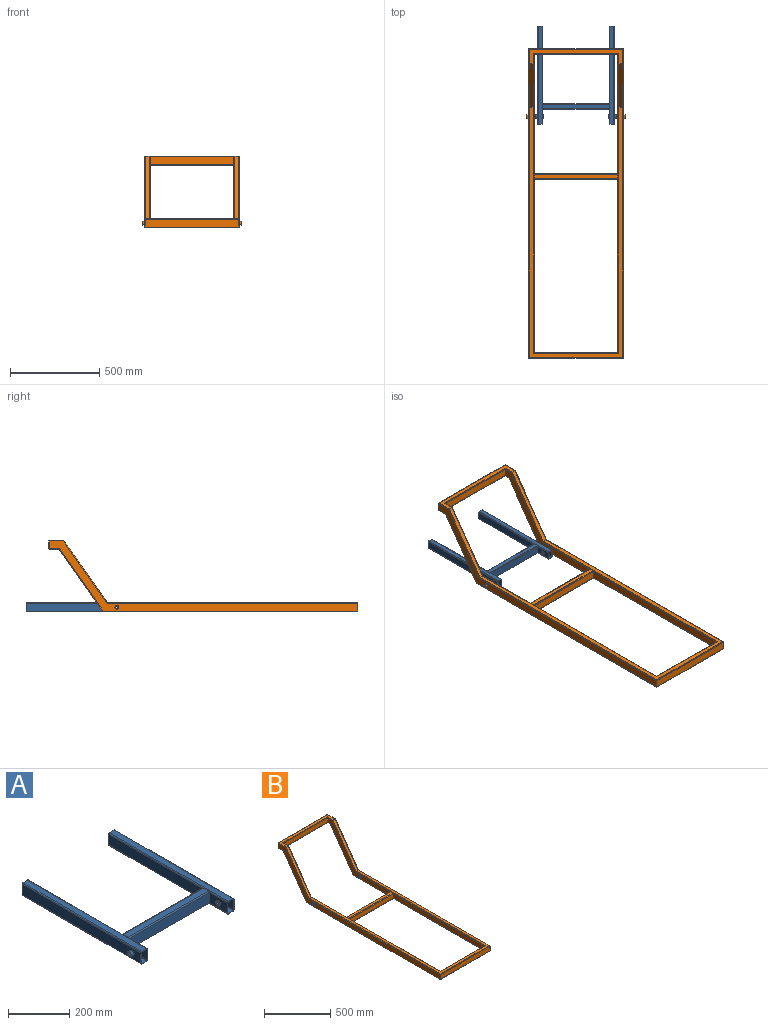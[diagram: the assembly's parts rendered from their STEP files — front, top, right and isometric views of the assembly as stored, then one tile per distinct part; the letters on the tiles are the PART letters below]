
ASSEMBLY  parts=2 mates=1
PART A: 72 faces, bbox 454x550x50 mm
  f0: plane 42x26mm, normal (1,0,0), area 1092mm2, adj f17,f19,f44,f48
  f1: plane 85x42mm, normal (1,0,0), area 3255.8mm2, adj f10,f17,f19,f56,f70
  f2: plane 550x22mm, normal (0,0,-1), area 12100mm2, adj f3,f9,f10,f11
  f3: cylinder r=2.02mm len=550mm, axis (0,1,0), area 1723.3mm2, adj f2,f4,f10,f11
  f4: plane 550x42mm, normal (1,0,0), area 22785.8mm2, adj f3,f5,f10,f11,f71
  f5: cylinder r=2.02mm len=550mm, axis (0,1,0), area 1723.3mm2, adj f4,f6,f10,f11
  f6: plane 550x22mm, normal (0,0,1), area 12100mm2, adj f5,f7,f10,f11
  f7: cylinder r=2.02mm len=550mm, axis (0,1,0), area 1723.3mm2, adj f6,f8,f10,f11
  f8: plane 550x42mm, normal (-1,0,0), area 22785.8mm2, adj f7,f9,f10,f11,f71
  f9: cylinder r=2.02mm len=550mm, axis (0,1,0), area 1723.3mm2, adj f2,f8,f10,f11
  f10: plane 50x30mm, normal (0,-1,0), area 293.8mm2, adj f1,f2,f3,f4,f5,f6,f7,f8
  f11: plane 50x30mm, normal (0,1,0), area 293.8mm2, adj f2,f3,f4,f5,f6,f7,f8,f9
  f12: plane 550x22mm, normal (0,0,-1), area 12100mm2, adj f10,f11,f13,f19
  f13: cylinder r=4mm len=550mm, axis (0,1,0), area 3455.7mm2, adj f10,f11,f12,f14
  f14: plane 550x42mm, normal (-1,0,0), area 22785.8mm2, adj f10,f11,f13,f15,f68
  f15: cylinder r=4mm len=550mm, axis (0,1,0), area 3455.7mm2, adj f10,f11,f14,f16
  f16: plane 550x22mm, normal (0,0,1), area 12100mm2, adj f10,f11,f15,f17
  f17: cylinder r=4mm len=550mm, axis (0,1,0), area 3455.7mm2, adj f0,f1,f10,f11,f16,f18,f58
  f18: plane 435x42mm, normal (1,0,0), area 18270mm2, adj f11,f17,f19,f52
  f19: cylinder r=4mm len=550mm, axis (0,1,0), area 3455.7mm2, adj f0,f1,f10,f11,f12,f18,f20
  f20: plane 30x4mm, normal (-1,0,0), area 62.9mm2, adj f19,f45,f46,f47,f50,f51,f57
  f21: plane 42x26mm, normal (-1,0,0), area 1092mm2, adj f34,f36,f44,f48
  f22: plane 435x42mm, normal (-1,0,0), area 18270mm2, adj f32,f34,f36,f52
  f23: plane 550x22mm, normal (0,0,-1), area 12100mm2, adj f24,f30,f31,f32
  f24: cylinder r=2.02mm len=550mm, axis (0,1,0), area 1723.3mm2, adj f23,f25,f31,f32
  f25: plane 550x42mm, normal (1,0,0), area 22785.8mm2, adj f24,f26,f31,f32,f65
  f26: cylinder r=2.02mm len=550mm, axis (0,1,0), area 1723.3mm2, adj f25,f27,f31,f32
  f27: plane 550x22mm, normal (0,0,1), area 12100mm2, adj f26,f28,f31,f32
  f28: cylinder r=2.02mm len=550mm, axis (0,1,0), area 1723.3mm2, adj f27,f29,f31,f32
  f29: plane 550x42mm, normal (-1,0,0), area 22785.8mm2, adj f28,f30,f31,f32,f65
  f30: cylinder r=2.02mm len=550mm, axis (0,1,0), area 1723.3mm2, adj f23,f29,f31,f32
  f31: plane 50x30mm, normal (0,-1,0), area 293.8mm2, adj f23,f24,f25,f26,f27,f28,f29,f30
  f32: plane 50x30mm, normal (0,1,0), area 293.8mm2, adj f22,f23,f24,f25,f26,f27,f28,f29
  f33: plane 550x22mm, normal (0,0,-1), area 12100mm2, adj f31,f32,f34,f40
  f34: cylinder r=4mm len=550mm, axis (0,1,0), area 3455.7mm2, adj f21,f22,f31,f32,f33,f35,f59
  f35: plane 85x42mm, normal (-1,0,0), area 3255.8mm2, adj f31,f34,f36,f56,f64
  f36: cylinder r=4mm len=550mm, axis (0,1,0), area 3455.7mm2, adj f21,f22,f31,f32,f35,f37,f41
  f37: plane 550x22mm, normal (0,0,1), area 12100mm2, adj f31,f32,f36,f38
  f38: cylinder r=4mm len=550mm, axis (0,1,0), area 3455.7mm2, adj f31,f32,f37,f39
  f39: plane 550x42mm, normal (1,0,0), area 22785.8mm2, adj f31,f32,f38,f40,f62
  f40: cylinder r=4mm len=550mm, axis (0,1,0), area 3455.7mm2, adj f31,f32,f33,f39
  f41: plane 30x4mm, normal (1,0,0), area 62.9mm2, adj f36,f42,f43,f49,f53,f54,f55
  f42: plane 370x22mm, normal (0,0,-1), area 8140mm2, adj f41,f43,f49,f58
  f43: cylinder r=2.02mm len=370mm, axis (1,0,0), area 1159.3mm2, adj f41,f42,f44,f58
  f44: plane 370x42mm, normal (0,-1,0), area 15540mm2, adj f0,f21,f43,f45
  f45: cylinder r=2.02mm len=370mm, axis (1,0,0), area 1159.3mm2, adj f20,f44,f46,f59
  f46: plane 370x22mm, normal (0,0,1), area 8140mm2, adj f20,f45,f47,f59
  f47: cylinder r=2.02mm len=370mm, axis (1,0,0), area 1159.3mm2, adj f20,f46,f48,f59
  f48: plane 370x42mm, normal (0,1,0), area 15540mm2, adj f0,f21,f47,f49
  f49: cylinder r=2.02mm len=370mm, axis (1,0,0), area 1159.3mm2, adj f41,f42,f48,f58
  f50: plane 370x22mm, normal (0,0,-1), area 8140mm2, adj f20,f51,f57,f59
  f51: cylinder r=4mm len=370mm, axis (1,0,0), area 2324.8mm2, adj f20,f50,f52,f59
  f52: plane 370x42mm, normal (0,1,0), area 15540mm2, adj f18,f22,f51,f53
  f53: cylinder r=4mm len=370mm, axis (1,0,0), area 2324.8mm2, adj f41,f52,f54,f58
  f54: plane 370x22mm, normal (0,0,1), area 8140mm2, adj f41,f53,f55,f58
  f55: cylinder r=4mm len=370mm, axis (1,0,0), area 2324.8mm2, adj f41,f54,f56,f58
  f56: plane 370x42mm, normal (0,-1,0), area 15540mm2, adj f1,f35,f55,f57
  f57: cylinder r=4mm len=370mm, axis (1,0,0), area 2324.8mm2, adj f20,f50,f56,f59
  f58: plane 30x4mm, normal (-1,0,0), area 62.9mm2, adj f17,f42,f43,f49,f53,f54,f55
  f59: plane 30x4mm, normal (1,0,0), area 62.9mm2, adj f34,f45,f46,f47,f50,f51,f57
  f60: plane 20x20mm, normal (1,0,0), area 201.1mm2, adj f62,f63
  f61: plane 20x20mm, normal (-1,0,0), area 201.1mm2, adj f63,f64
  f62: cylinder r=10mm len=20mm, axis (1,0,0), area 754mm2, adj f39,f60
  f63: cylinder r=6mm len=45mm, axis (1,0,0), area 1696.5mm2, adj f60,f61
  f64: cylinder r=10mm len=20mm, axis (1,0,0), area 188.5mm2, adj f35,f61
  f65: cylinder r=10mm len=26mm, axis (1,0,0), area 1633.6mm2, adj f25,f29
  f66: plane 20x20mm, normal (-1,0,0), area 201.1mm2, adj f68,f69
  f67: plane 20x20mm, normal (1,0,0), area 201.1mm2, adj f69,f70
  f68: cylinder r=10mm len=20mm, axis (-1,0,0), area 754mm2, adj f14,f66
  f69: cylinder r=6mm len=45mm, axis (-1,0,0), area 1696.5mm2, adj f66,f67
  f70: cylinder r=10mm len=20mm, axis (-1,0,0), area 188.5mm2, adj f1,f67
  f71: cylinder r=10mm len=26mm, axis (-1,0,0), area 1633.6mm2, adj f4,f8
PART B: 132 faces, bbox 550x1730x400 mm
  f0: plane 42x26mm, normal (1,0,0), area 1092mm2, adj f8,f9,f26,f30
  f1: plane 970x42mm, normal (1,0,0), area 40740mm2, adj f8,f9,f18,f71
  f2: plane 670x392mm, normal (1,0,0), area 35478.2mm2, adj f8,f9,f22,f34,f35,f40,f41,f45
  f3: plane 1424.01x522mm, normal (0,0,-1), area 73172.6mm2, adj f4,f9,f39,f61,f62,f66,f70,f75
  f4: cylinder r=4mm len=1428.01mm, axis (0,1,0), area 8958.5mm2, adj f3,f5,f38,f75
  f5: plane 1730x392mm, normal (-1,0,0), area 79998.2mm2, adj f4,f6,f37,f38,f42,f43,f48,f74
  f6: cylinder r=4mm len=1404.07mm, axis (0,1,0), area 8804.5mm2, adj f5,f7,f37,f73
  f7: plane 1397.99x522mm, normal (0,0,1), area 72027.4mm2, adj f6,f8,f36,f58,f63,f64,f72,f73
  f8: cylinder r=4mm len=1378.07mm, axis (0,1,0), area 8634.3mm2, adj f0,f1,f2,f7,f16,f35,f72
  f9: cylinder r=4mm len=1402.01mm, axis (0,1,0), area 8788.3mm2, adj f0,f1,f2,f3,f34,f70,f76
  f10: cylinder r=10mm len=20mm, axis (1,0,0), area 314.2mm2, adj f13,f68
  f11: cylinder r=6mm len=45mm, axis (1,0,0), area 1696.5mm2, adj f13,f14
  f12: cylinder r=10mm len=20mm, axis (1,0,0), area 628.3mm2, adj f14,f65
  f13: plane 20x20mm, normal (-1,0,0), area 201.1mm2, adj f10,f11
  f14: plane 20x20mm, normal (1,0,0), area 201.1mm2, adj f11,f12
  f15: plane 30x4mm, normal (1,0,0), area 62.9mm2, adj f19,f20,f21,f25,f31,f32,f63
  f16: plane 30x4mm, normal (-1,0,0), area 62.9mm2, adj f8,f19,f20,f21,f25,f31,f32
  f17: cylinder r=4mm len=470mm, axis (1,0,0), area 2953.1mm2, adj f18,f24,f33,f76
  f18: plane 470x42mm, normal (0,-1,0), area 19740mm2, adj f1,f17,f19,f67
  f19: cylinder r=4mm len=470mm, axis (1,0,0), area 2953.1mm2, adj f15,f16,f18,f20
  f20: plane 470x22mm, normal (0,0,1), area 10340mm2, adj f15,f16,f19,f21
  f21: cylinder r=4mm len=470mm, axis (1,0,0), area 2953.1mm2, adj f15,f16,f20,f22
  f22: plane 470x42mm, normal (0,1,0), area 19740mm2, adj f2,f21,f23,f68
  f23: cylinder r=4mm len=470mm, axis (1,0,0), area 2953.1mm2, adj f22,f24,f33,f76
  f24: plane 470x22mm, normal (0,0,-1), area 10340mm2, adj f17,f23,f33,f76
  f25: cylinder r=2.02mm len=470mm, axis (1,0,0), area 1472.6mm2, adj f15,f16,f26,f32
  f26: plane 470x42mm, normal (0,1,0), area 19740mm2, adj f0,f25,f27,f69
  f27: cylinder r=2.02mm len=470mm, axis (1,0,0), area 1472.6mm2, adj f26,f28,f33,f76
  f28: plane 470x22mm, normal (0,0,1), area 10340mm2, adj f27,f29,f33,f76
  f29: cylinder r=2.02mm len=470mm, axis (1,0,0), area 1472.6mm2, adj f28,f30,f33,f76
  f30: plane 470x42mm, normal (0,-1,0), area 19740mm2, adj f0,f29,f31,f69
  f31: cylinder r=2.02mm len=470mm, axis (1,0,0), area 1472.6mm2, adj f15,f16,f30,f32
  f32: plane 470x22mm, normal (0,0,-1), area 10340mm2, adj f15,f16,f25,f31
  f33: plane 30x4mm, normal (1,0,0), area 62.9mm2, adj f17,f23,f24,f27,f28,f29,f62
  f34: cylinder r=4mm len=354mm, axis (0,0.57,0.82), area 2684.6mm2, adj f2,f9,f39,f40
  f35: cylinder r=4mm len=354mm, axis (0,0.57,0.82), area 2684.6mm2, adj f2,f8,f36,f41
  f36: plane 350x245.07mm, normal (0,-0.82,0.57), area 9400mm2, adj f7,f35,f37,f52
  f37: cylinder r=4mm len=354mm, axis (0,0.57,0.82), area 2684.6mm2, adj f5,f6,f36,f42
  f38: cylinder r=4mm len=354mm, axis (0,0.57,0.82), area 2684.6mm2, adj f4,f5,f39,f43
  f39: plane 350x245.07mm, normal (0,0.82,-0.57), area 9400mm2, adj f3,f34,f38,f55
  f40: cylinder r=4mm len=33mm, axis (0,1,0), area 183mm2, adj f2,f34,f44,f55
  f41: cylinder r=4mm len=56.94mm, axis (0,1,0), area 337mm2, adj f2,f35,f46,f52
  f42: cylinder r=4mm len=82.94mm, axis (0,1,0), area 507.2mm2, adj f5,f37,f47,f52
  f43: cylinder r=4mm len=59mm, axis (0,1,0), area 353.2mm2, adj f5,f38,f49,f55
  f44: cylinder r=4mm len=478mm, axis (1,0,0), area 2971.3mm2, adj f40,f45,f50,f55
  f45: plane 470x42mm, normal (0,-1,0), area 19740mm2, adj f2,f44,f46,f68
  f46: cylinder r=4mm len=478mm, axis (1,0,0), area 2971.3mm2, adj f41,f45,f51,f52
  f47: cylinder r=4mm len=530mm, axis (1,0,0), area 3311.8mm2, adj f42,f48,f52,f53
  f48: plane 530x42mm, normal (0,1,0), area 22260mm2, adj f5,f47,f49,f65
  f49: cylinder r=4mm len=530mm, axis (1,0,0), area 3311.8mm2, adj f43,f48,f54,f55
  f50: cylinder r=4mm len=33mm, axis (0,-1,0), area 183mm2, adj f44,f55,f56,f68
  f51: cylinder r=4mm len=56.94mm, axis (0,-1,0), area 337mm2, adj f46,f52,f57,f68
  f52: plane 522x78.94mm, normal (0,0,1), area 13989.4mm2, adj f36,f41,f42,f46,f47,f51,f53,f58
  f53: cylinder r=4mm len=82.94mm, axis (0,-1,0), area 507.2mm2, adj f47,f52,f59,f65
  f54: cylinder r=4mm len=59mm, axis (0,-1,0), area 353.2mm2, adj f49,f55,f60,f65
  f55: plane 522x52.91mm, normal (0,0,-1), area 12844.2mm2, adj f39,f40,f43,f44,f49,f50,f54,f61
  f56: cylinder r=4mm len=354mm, axis (0,-0.57,-0.82), area 2684.6mm2, adj f50,f61,f62,f68
  f57: cylinder r=4mm len=354mm, axis (0,-0.57,-0.82), area 2684.6mm2, adj f51,f58,f63,f68
  f58: plane 350x245.07mm, normal (0,-0.82,0.57), area 9400mm2, adj f7,f52,f57,f59
  f59: cylinder r=4mm len=354mm, axis (0,-0.57,-0.82), area 2684.6mm2, adj f53,f58,f64,f65
  f60: cylinder r=4mm len=354mm, axis (0,-0.57,-0.82), area 2684.6mm2, adj f54,f61,f65,f66
  f61: plane 350x245.07mm, normal (0,0.82,-0.57), area 9400mm2, adj f3,f55,f56,f60
  f62: cylinder r=4mm len=1402.01mm, axis (0,-1,0), area 8788.3mm2, adj f3,f33,f56,f67,f68,f69,f70
  f63: cylinder r=4mm len=1378.07mm, axis (0,-1,0), area 8634.3mm2, adj f7,f15,f57,f67,f68,f69,f72
  f64: cylinder r=4mm len=1404.07mm, axis (0,-1,0), area 8804.5mm2, adj f7,f59,f65,f73
  f65: plane 1730x392mm, normal (1,0,0), area 79998.2mm2, adj f12,f48,f53,f54,f59,f60,f64,f66
  f66: cylinder r=4mm len=1428.01mm, axis (0,-1,0), area 8958.5mm2, adj f3,f60,f65,f75
  f67: plane 970x42mm, normal (-1,0,0), area 40740mm2, adj f18,f62,f63,f71
  f68: plane 670x392mm, normal (-1,0,0), area 35478.2mm2, adj f10,f22,f45,f50,f51,f56,f57,f62
  f69: plane 42x26mm, normal (-1,0,0), area 1092mm2, adj f26,f30,f62,f63
  f70: cylinder r=4mm len=478mm, axis (-1,0,0), area 2971.3mm2, adj f3,f9,f62,f71
  f71: plane 470x42mm, normal (0,1,0), area 19740mm2, adj f1,f67,f70,f72
  f72: cylinder r=4mm len=478mm, axis (-1,0,0), area 2971.3mm2, adj f7,f8,f63,f71
  f73: cylinder r=4mm len=530mm, axis (-1,0,0), area 3311.8mm2, adj f6,f7,f64,f74
  f74: plane 530x42mm, normal (0,-1,0), area 22260mm2, adj f5,f65,f73,f75
  f75: cylinder r=4mm len=530mm, axis (-1,0,0), area 3311.8mm2, adj f3,f4,f66,f74
  f76: plane 30x4mm, normal (-1,0,0), area 62.9mm2, adj f9,f17,f23,f24,f27,f28,f29
  f77: plane 20x20mm, normal (-1,0,0), area 201.1mm2, adj f79,f80
  f78: plane 20x20mm, normal (1,0,0), area 201.1mm2, adj f80,f81
  f79: cylinder r=10mm len=20mm, axis (-1,0,0), area 628.3mm2, adj f5,f77
  f80: cylinder r=6mm len=45mm, axis (-1,0,0), area 1696.5mm2, adj f77,f78
  f81: cylinder r=10mm len=20mm, axis (-1,0,0), area 314.2mm2, adj f2,f78
  f82: cylinder r=10mm len=26mm, axis (-1,0,0), area 1633.6mm2, adj f120,f131
  f83: cylinder r=2.02mm len=352mm, axis (0,-0.57,-0.82), area 1338.8mm2, adj f85,f86,f87,f100
  f84: cylinder r=2.02mm len=352mm, axis (0,-0.57,-0.82), area 1338.8mm2, adj f93,f95,f96,f100
  f85: cylinder r=2.02mm len=1424.97mm, axis (0,-1,0), area 4461.3mm2, adj f83,f100,f102,f104
  f86: cylinder r=2.02mm len=57mm, axis (0,-1,0), area 174.2mm2, adj f83,f100,f101,f106
  f87: plane 350x245.07mm, normal (0,-0.82,0.57), area 9400mm2, adj f83,f90,f104,f106
  f88: cylinder r=2.02mm len=352mm, axis (0,-0.57,-0.82), area 1338.8mm2, adj f94,f96,f97,f108
  f89: cylinder r=2.02mm len=33mm, axis (0,-1,0), area 97.3mm2, adj f90,f106,f107,f108
  f90: cylinder r=2.02mm len=352mm, axis (0,-0.57,-0.82), area 1338.8mm2, adj f87,f89,f91,f108
  f91: cylinder r=2.02mm len=1400.97mm, axis (0,-1,0), area 4384.5mm2, adj f90,f103,f104,f108
  f92: cylinder r=10mm len=26mm, axis (1,0,0), area 1633.6mm2, adj f100,f108
  f93: cylinder r=2.02mm len=79.9mm, axis (0,-1,0), area 246.9mm2, adj f84,f99,f100,f109
  f94: cylinder r=2.02mm len=55.9mm, axis (0,-1,0), area 170mm2, adj f88,f108,f109,f110
  f95: cylinder r=2.02mm len=1402.07mm, axis (0,-1,0), area 4388.7mm2, adj f84,f98,f100,f121
  f96: plane 350x245.07mm, normal (0,0.82,-0.57), area 9400mm2, adj f84,f88,f109,f121
  f97: cylinder r=2.02mm len=1378.07mm, axis (0,-1,0), area 4311.8mm2, adj f88,f108,f121,f122
  f98: cylinder r=2.02mm len=526mm, axis (-1,0,0), area 1643.5mm2, adj f95,f112,f113,f121
  f99: cylinder r=2.02mm len=526mm, axis (1,0,0), area 1643.5mm2, adj f93,f109,f115,f116
  f100: plane 1726x392mm, normal (-1,0,0), area 79830.2mm2, adj f83,f84,f85,f86,f92,f93,f95,f112
  f101: cylinder r=2.02mm len=526mm, axis (1,0,0), area 1643.5mm2, adj f86,f106,f116,f117
  f102: cylinder r=2.02mm len=526mm, axis (-1,0,0), area 1643.5mm2, adj f85,f104,f112,f119
  f103: cylinder r=2.02mm len=478mm, axis (-1,0,0), area 1489.7mm2, adj f91,f104,f123,f124
  f104: plane 1422.97x522mm, normal (0,0,1), area 73126.8mm2, adj f85,f87,f91,f102,f103,f105,f119,f124
  f105: plane 350x245.07mm, normal (0,-0.82,0.57), area 9400mm2, adj f104,f106,f118,f125
  f106: plane 522x53.95mm, normal (0,0,1), area 12890mm2, adj f86,f87,f89,f101,f105,f107,f117,f126
  f107: cylinder r=2.02mm len=478mm, axis (1,0,0), area 1489.7mm2, adj f89,f106,f126,f127
  f108: plane 1674x392mm, normal (1,0,0), area 77646.2mm2, adj f88,f89,f90,f91,f92,f94,f97,f123
  f109: plane 522x77.9mm, normal (0,0,-1), area 13943.6mm2, adj f93,f94,f96,f99,f110,f111,f115,f128
  f110: cylinder r=2.02mm len=478mm, axis (1,0,0), area 1489.7mm2, adj f94,f109,f127,f128
  f111: plane 350x245.07mm, normal (0,0.82,-0.57), area 9400mm2, adj f109,f114,f121,f129
  f112: plane 526x42mm, normal (0,1,0), area 22092mm2, adj f98,f100,f102,f120
  f113: cylinder r=2.02mm len=1402.07mm, axis (0,1,0), area 4388.7mm2, adj f98,f114,f120,f121
  f114: cylinder r=2.02mm len=352mm, axis (0,0.57,0.82), area 1338.8mm2, adj f111,f113,f115,f120
  f115: cylinder r=2.02mm len=79.9mm, axis (0,1,0), area 246.9mm2, adj f99,f109,f114,f120
  f116: plane 526x42mm, normal (0,-1,0), area 22092mm2, adj f99,f100,f101,f120
  f117: cylinder r=2.02mm len=57mm, axis (0,1,0), area 174.2mm2, adj f101,f106,f118,f120
  f118: cylinder r=2.02mm len=352mm, axis (0,0.57,0.82), area 1338.8mm2, adj f105,f117,f119,f120
  f119: cylinder r=2.02mm len=1424.97mm, axis (0,1,0), area 4461.3mm2, adj f102,f104,f118,f120
  f120: plane 1726x392mm, normal (1,0,0), area 79830.2mm2, adj f82,f112,f113,f114,f115,f116,f117,f118
  f121: plane 1399.03x522mm, normal (0,0,-1), area 72073.2mm2, adj f95,f96,f97,f98,f111,f113,f122,f130
  f122: cylinder r=2.02mm len=478mm, axis (-1,0,0), area 1489.7mm2, adj f97,f121,f123,f130
  f123: plane 474x42mm, normal (0,-1,0), area 19908mm2, adj f103,f108,f122,f131
  f124: cylinder r=2.02mm len=1400.97mm, axis (0,1,0), area 4384.5mm2, adj f103,f104,f125,f131
  f125: cylinder r=2.02mm len=352mm, axis (0,0.57,0.82), area 1338.8mm2, adj f105,f124,f126,f131
  f126: cylinder r=2.02mm len=33mm, axis (0,1,0), area 97.3mm2, adj f106,f107,f125,f131
  f127: plane 474x42mm, normal (0,1,0), area 19908mm2, adj f107,f108,f110,f131
  f128: cylinder r=2.02mm len=55.9mm, axis (0,1,0), area 170mm2, adj f109,f110,f129,f131
  f129: cylinder r=2.02mm len=352mm, axis (0,0.57,0.82), area 1338.8mm2, adj f111,f128,f130,f131
  f130: cylinder r=2.02mm len=1378.07mm, axis (0,1,0), area 4311.8mm2, adj f121,f122,f129,f131
  f131: plane 1674x392mm, normal (-1,0,0), area 77646.2mm2, adj f82,f123,f124,f125,f126,f127,f128,f129
PLACE A t=(104.9,-447.42,262.26)mm
PLACE B t=(104.9,-447.42,262.26)mm
MATE revolute A.f68 <-> B.f79  axis (-1,0,0) through (-122.1,744.5,262.26)mm
